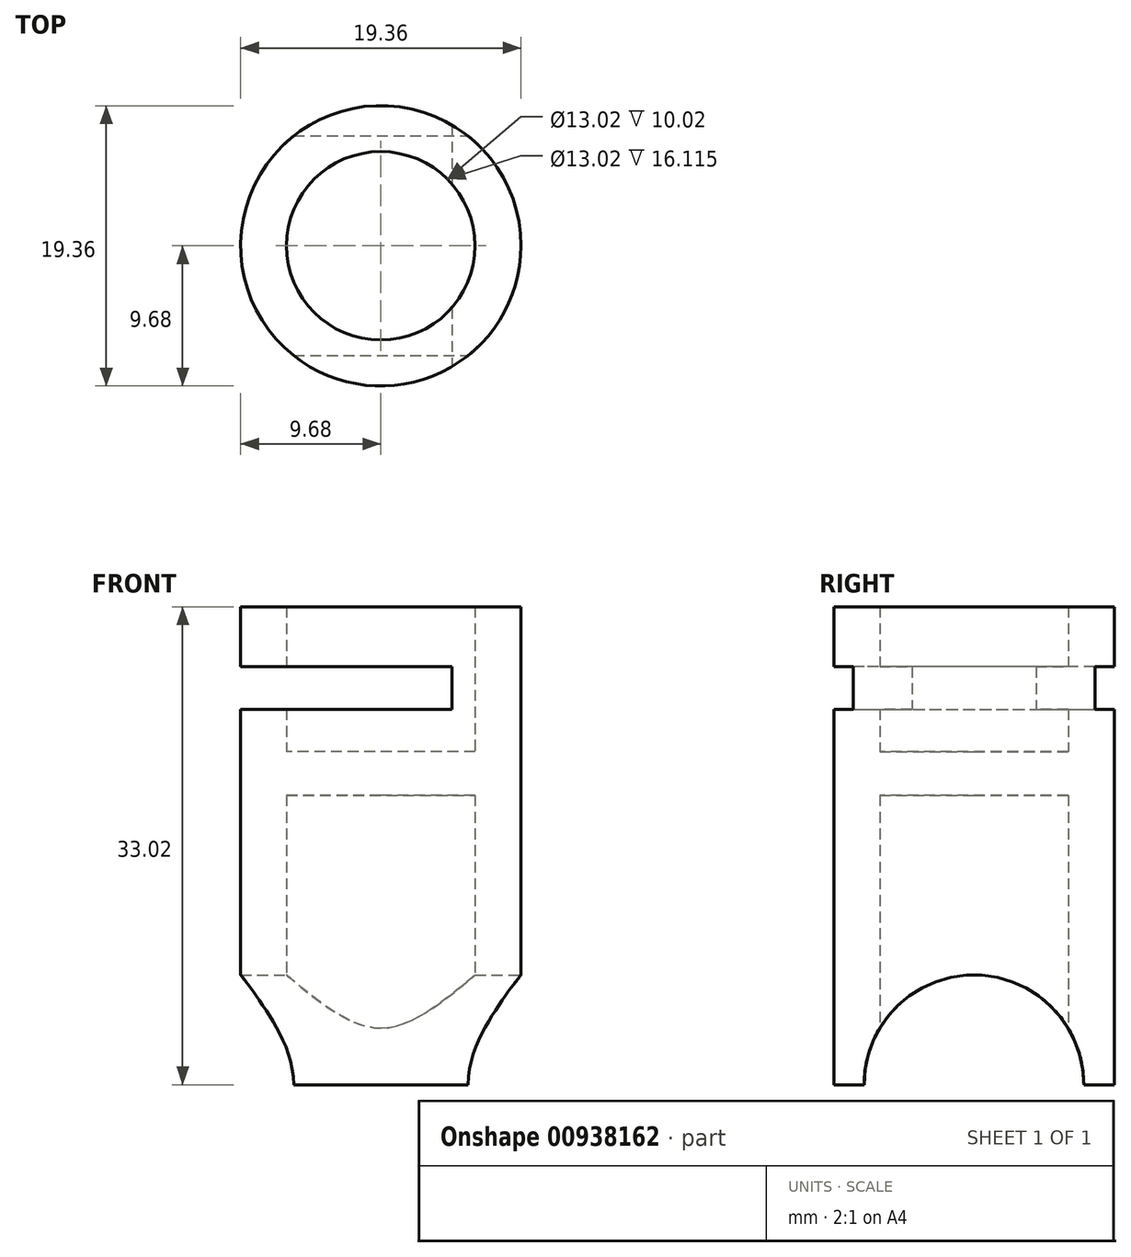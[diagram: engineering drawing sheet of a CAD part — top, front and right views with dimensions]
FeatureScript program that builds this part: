
annotation { "Feature Type Name" : "Feature", "Feature Type Description" : "" }
export const myFeature = defineFeature(function(context is Context, id is Id, definition is map)
    precondition{}
    {
        {
            var Q0;
            Q0=qCreatedBy(makeId("Top.planeOp"),FACE);
            var sketch = newSketch(context, id + "F0", { "sketchPlane" : qUnion([Q0])});
            skCircle(sketch, "E0", {"center": v(0, 0) * mm, "radius": 6.5 * mm});
            skCircle(sketch, "E1", {"center": v(0, 0) * mm, "radius": 9.68 * mm});
            skSolve(sketch);
        }
        {
            var Q0;
            Q0=makeQuery(id+"F0.imprint","IMPRINT",FACE,{"disambiguationData":[TD([[makeQuery(id+"F0.imprint","IMPRINT",EDGE,{"derivedFrom":sQuery(id+"F0.wireOp",EDGE,"E0")}),-1.0]])]});
            extrude(context, id + "F1", {"entities" : qUnion([Q0]), "depth" : 33.02 * mm, "offsetDistance" : 25 * mm});
        }
        {
            var Q0;
            Q0=qCreatedBy(makeId("Right.planeOp"),FACE);
            var sketch = newSketch(context, id + "F2", { "sketchPlane" : qUnion([Q0])});
            skArc(sketch, "E2", {"start": v(-7.59, 0) * mm, "mid": v(0, 7.59) * mm, "end": v(7.59, 0) * mm});
            skLineSegment(sketch, "E3", {"start": v(-7.59, 0) * mm, "end": v(7.59, 0) * mm});
            skSolve(sketch);
        }
        {
            var Q0;
            Q0=qSketchRegion(id+"F2",true);
            extrude(context, id + "F3", {"entities" : qUnion([Q0]), "operationType" : NewBodyOperationType.REMOVE, "oppositeDirection" : true, "depth" : 25 * mm, "offsetDistance" : 25 * mm});
        }
        {
            var Q0;
            Q0=qSketchRegion(id+"F2",true);
            extrude(context, id + "F4", {"entities" : qUnion([Q0]), "operationType" : NewBodyOperationType.REMOVE, "depth" : 54.6 * mm, "offsetDistance" : 25 * mm});
        }
        {
            var Q0;
            Q0=qCreatedBy(makeId("Top.planeOp"),FACE);
            cPlane(context, id + "F5", {"entities" : qUnion([Q0]), "cplaneType" : CPlaneType.OFFSET, "offset" : 20 * mm, "width" : 150 * mm, "height" : 150 * mm});
        }
        {
            var Q0;
            Q0=qCreatedBy(id+"F5.planeOp",FACE);
            var sketch = newSketch(context, id + "F6", { "sketchPlane" : qUnion([Q0])});
            skCircle(sketch, "E4", {"center": v(0, 0) * mm, "radius": 6.5 * mm});
            skSolve(sketch);
        }
        {
            var Q0;
            Q0 = qSketchRegion(id + "F6", true);
            extrude(context, id + "F7", {"entities" : qUnion([Q0]), "operationType" : NewBodyOperationType.ADD, "depth" : 3 * mm, "offsetDistance" : 25 * mm});
        }
        {
            var Q0;
            Q0=qCreatedBy(makeId("Right.planeOp"),FACE);
            var sketch = newSketch(context, id + "F8", { "sketchPlane" : qUnion([Q0])});
            skLineSegment(sketch, "E5", {"start": v(10.1, 28.87) * mm, "end": v(-10.25, 28.87) * mm});
            skLineSegment(sketch, "E6", {"start": v(-10.25, 28.87) * mm, "end": v(-10.25, 25.93) * mm});
            skLineSegment(sketch, "E7", {"start": v(-10.25, 25.93) * mm, "end": v(10.25, 25.93) * mm});
            skLineSegment(sketch, "E8", {"start": v(10.25, 25.93) * mm, "end": v(10.1, 28.87) * mm});
            skSolve(sketch);
        }
        {
            var Q0;
            Q0=makeQuery(id+"F8.imprint","IMPRINT",FACE,{"disambiguationData":[TD([[makeQuery(id+"F8.imprint","IMPRINT",EDGE,{"derivedFrom":sQuery(id+"F8.wireOp",EDGE,"E5")}),1.0]])]});
            extrude(context, id + "F9", {"entities" : qUnion([Q0]), "operationType" : NewBodyOperationType.REMOVE, "oppositeDirection" : true, "depth" : 25 * mm, "offsetDistance" : 25 * mm});
        }
        {
            var Q0;
            Q0 = qSketchRegion(id + "F8", true);
            extrude(context, id + "F10", {"entities" : qUnion([Q0]), "operationType" : NewBodyOperationType.REMOVE, "depth" : 4.9 * mm, "offsetDistance" : 25 * mm});
        }
    });
